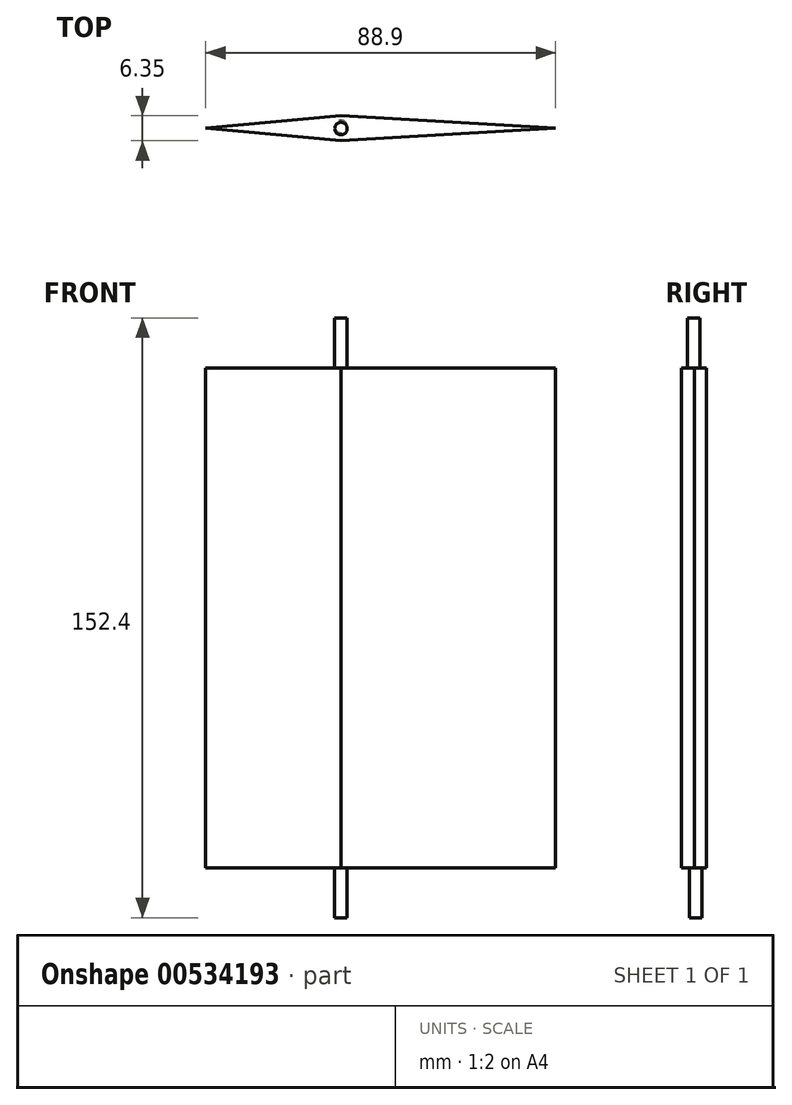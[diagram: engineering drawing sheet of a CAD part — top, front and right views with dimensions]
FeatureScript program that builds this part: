
annotation { "Feature Type Name" : "Feature", "Feature Type Description" : "" }
export const myFeature = defineFeature(function(context is Context, id is Id, definition is map)
    precondition{}
    {
        {
            var Q0;
            Q0=qCreatedBy(makeId("Top.planeOp"),FACE);
            var sketch = newSketch(context, id + "F0", { "sketchPlane" : qUnion([Q0])});
            skLineSegment(sketch, "E0", {"start": v(-34.38, 29.53) * mm, "end": v(0, 32.66) * mm});
            skLineSegment(sketch, "E1", {"start": v(-34.38, 29.53) * mm, "end": v(0, 26.31) * mm});
            skLineSegment(sketch, "E2", {"start": v(0, 26.31) * mm, "end": v(54.52, 29.53) * mm});
            skLineSegment(sketch, "E3", {"start": v(0, 32.66) * mm, "end": v(54.52, 29.53) * mm});
            skSolve(sketch);
        }
        {
            var Q0;
            Q0 = qSketchRegion(id + "F0", true);
            var Q1;
            Q1=makeQuery(id+"F0.imprint","IMPRINT",FACE,{"disambiguationData":[TD([[makeQuery(id+"F0.imprint","IMPRINT",EDGE,{"derivedFrom":sQuery(id+"F0.wireOp",EDGE,"E0")}),-1.0]])]});
            extrude(context, id + "F1", {"entities" : qUnion([Q0, Q1]), "depth" : 127 * mm, "offsetDistance" : 25.4 * mm});
        }
        {
            var Q0;
            Q0=makeQuery(id+"F1.opExtrude","CAP_FACE",FACE,{"disambiguationData":[OSD([sQuery(id+"F0.wireOp",EDGE,"E0"),sQuery(id+"F0.wireOp",EDGE,"E1"),sQuery(id+"F0.wireOp",EDGE,"E2"),sQuery(id+"F0.wireOp",EDGE,"E3")])],"isStart":true});
            var sketch = newSketch(context, id + "F2", { "sketchPlane" : qUnion([Q0])});
            skCircle(sketch, "E4", {"center": v(0, -29.96) * mm, "radius": 1.59 * mm});
            skSolve(sketch);
        }
        {
            var Q0;
            Q0=makeQuery(id+"F2.imprint","IMPRINT",FACE,{"disambiguationData":[TD([[makeQuery(id+"F2.imprint","IMPRINT",EDGE,{"derivedFrom":sQuery(id+"F2.wireOp",EDGE,"E4")}),1.0]])]});
            extrude(context, id + "F3", {"entities" : qUnion([Q0]), "operationType" : NewBodyOperationType.ADD, "depth" : 12.7 * mm, "offsetDistance" : 25.4 * mm});
        }
        {
            var Q0;
            Q0=makeQuery(id+"F1.opExtrude","CAP_FACE",FACE,{"disambiguationData":[OSD([sQuery(id+"F0.wireOp",EDGE,"E0"),sQuery(id+"F0.wireOp",EDGE,"E1"),sQuery(id+"F0.wireOp",EDGE,"E2"),sQuery(id+"F0.wireOp",EDGE,"E3")])],"isStart":false});
            var sketch = newSketch(context, id + "F4", { "sketchPlane" : qUnion([Q0])});
            skCircle(sketch, "E5", {"center": v(0, 29.42) * mm, "radius": 1.59 * mm});
            skSolve(sketch);
        }
        {
            var Q0;
            Q0 = qSketchRegion(id + "F4", true);
            extrude(context, id + "F5", {"entities" : qUnion([Q0]), "operationType" : NewBodyOperationType.ADD, "depth" : 12.7 * mm, "offsetDistance" : 25.4 * mm});
        }
    });
